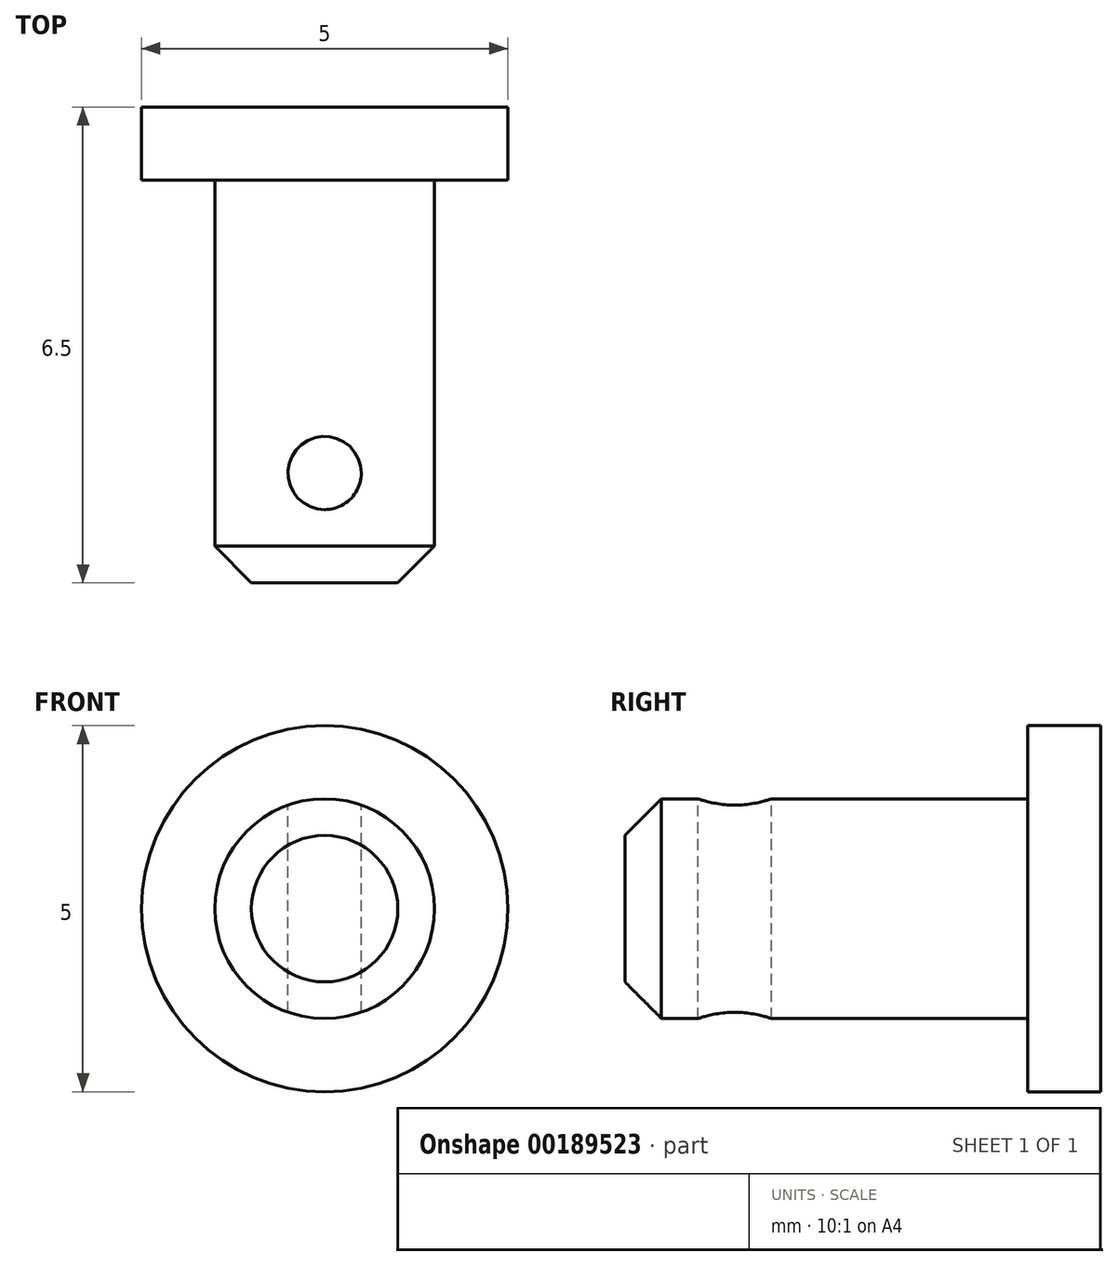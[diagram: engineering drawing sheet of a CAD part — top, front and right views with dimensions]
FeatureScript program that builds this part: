
annotation { "Feature Type Name" : "Feature", "Feature Type Description" : "" }
export const myFeature = defineFeature(function(context is Context, id is Id, definition is map)
    precondition{}
    {
        {
            var Q0;
            Q0=qCreatedBy(makeId("Front.planeOp"),FACE);
            var sketch = newSketch(context, id + "F0", { "sketchPlane" : qUnion([Q0])});
            skCircle(sketch, "E0", {"center": v(0, 0) * mm, "radius": 2.5 * mm});
            skCircle(sketch, "E1", {"center": v(0, 0) * mm, "radius": 1.5 * mm});
            skSolve(sketch);
        }
        {
            var Q0;
            Q0=makeQuery(id+"F0.imprint","IMPRINT",FACE,{"disambiguationData":[TD([[makeQuery(id+"F0.imprint","IMPRINT",EDGE,{"derivedFrom":sQuery(id+"F0.wireOp",EDGE,"E1")}),1.0]])]});
            extrude(context, id + "F1", {"entities" : qUnion([Q0]), "depth" : 5.5 * mm});
        }
        {
            var Q0;
            Q0=makeQuery(id+"F0.imprint","IMPRINT",FACE,{"disambiguationData":[TD([[makeQuery(id+"F0.imprint","IMPRINT",EDGE,{"derivedFrom":sQuery(id+"F0.wireOp",EDGE,"E0")}),1.0]])]});
            var Q1;
            Q1=makeQuery(id+"F0.imprint","IMPRINT",FACE,{"disambiguationData":[TD([[makeQuery(id+"F0.imprint","IMPRINT",EDGE,{"derivedFrom":sQuery(id+"F0.wireOp",EDGE,"E1")}),1.0]])]});
            extrude(context, id + "F2", {"entities" : qUnion([Q0, Q1]), "operationType" : NewBodyOperationType.ADD, "oppositeDirection" : true, "depth" : 1 * mm});
        }
        {
            var Q0;
            Q0=makeQuery(id+"F1.opExtrude","CAP_EDGE",EDGE,{"disambiguationData":[OSD([sQuery(id+"F0.wireOp",EDGE,"E1")])],"isStart":false});
            chamfer(context, id + "F3", {"entities" : qUnion([Q0]), "width" : 0.5 * mm, "tangentPropagation" : true});
        }
        {
            var Q0;
            Q0=qCreatedBy(makeId("Top.planeOp"),FACE);
            var sketch = newSketch(context, id + "F4", { "sketchPlane" : qUnion([Q0])});
            skCircle(sketch, "E2", {"center": v(0, -4) * mm, "radius": 0.5 * mm});
            skSolve(sketch);
        }
        {
            var Q0;
            Q0=makeQuery(id+"F4.imprint","IMPRINT",FACE,{"disambiguationData":[TD([[makeQuery(id+"F4.imprint","IMPRINT",EDGE,{"derivedFrom":sQuery(id+"F4.wireOp",EDGE,"E2")}),1.0]])]});
            extrude(context, id + "F5", {"entities" : qUnion([Q0]), "operationType" : NewBodyOperationType.REMOVE, "endBound" : BoundingType.SYMMETRIC, "oppositeDirection" : true, "depth" : 25 * mm});
        }
    });
